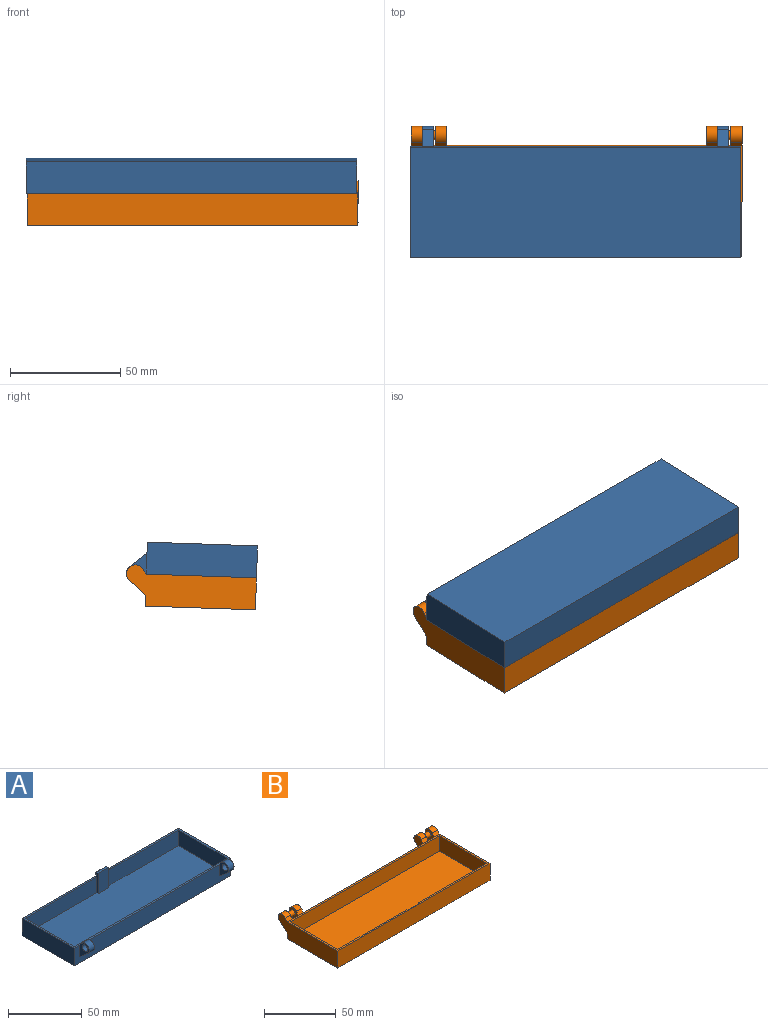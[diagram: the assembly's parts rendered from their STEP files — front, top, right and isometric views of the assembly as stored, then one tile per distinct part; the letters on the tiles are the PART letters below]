
ASSEMBLY  parts=2 mates=1
PART A: 32 faces, bbox 150x59x18.5 mm
  f0: plane 10x2mm, normal (0,1,0), area 20mm2, adj f1,f11,f13,f17
  f1: plane 150x50mm, normal (0,0,1), area 591mm2, adj f0,f2,f3,f4,f5,f7,f8,f9
  f2: plane 150x14.5mm, normal (0,-1,0), area 2080.2mm2, adj f1,f3,f5,f6,f22,f23,f24,f29
  f3: plane 50x14.5mm, normal (1,0,0), area 725mm2, adj f1,f2,f4,f6
  f4: plane 150x14.5mm, normal (0,1,0), area 2175mm2, adj f1,f3,f5,f6
  f5: plane 50x14.5mm, normal (-1,0,0), area 725mm2, adj f1,f2,f4,f6
  f6: plane 150x50mm, normal (0,0,-1), area 7500mm2, adj f2,f3,f4,f5
  f7: plane 47x13mm, normal (-1,0,0), area 611mm2, adj f1,f8,f14,f15
  f8: plane 147x13mm, normal (0,1,0), area 1911mm2, adj f1,f7,f9,f15
  f9: plane 47x13mm, normal (1,0,0), area 611mm2, adj f1,f8,f10,f15
  f10: plane 68.5x13mm, normal (0,-1,0), area 890.5mm2, adj f1,f9,f11,f15
  f11: plane 17x2.5mm, normal (-1,0,0), area 27.1mm2, adj f0,f10,f12,f15,f16,f17
  f12: plane 17x10mm, normal (0,-1,0), area 170mm2, adj f11,f13,f15,f16
  f13: plane 17x2.5mm, normal (1,0,0), area 27.1mm2, adj f0,f12,f14,f15,f16,f17
  f14: plane 68.5x13mm, normal (0,-1,0), area 890.5mm2, adj f1,f7,f13,f15
  f15: plane 147x47mm, normal (0,0,1), area 6894mm2, adj f7,f8,f9,f10,f11,f12,f13,f14
  f16: plane 10x1.5mm, normal (0,0,1), area 15mm2, adj f11,f12,f13,f17
  f17: cylinder r=1mm len=10mm, axis (1,0,0), area 31.4mm2, adj f0,f11,f13,f16
  f18: plane 5x0mm, normal (0,1,0), area 0mm2, adj f1,f19,f23,f24
  f19: plane 5x2.4mm, normal (0,0.8,0.6), area 15mm2, adj f18,f20,f23,f24
  f20: cylinder r=4mm len=7.2mm, axis (1,0,0), area 67.3mm2, adj f19,f22,f23,f24
  f21: cylinder r=2.5mm len=5mm, axis (1,0,0), area 78.5mm2, adj f23,f24
  f22: plane 7.59x6.42mm, normal (0,-0.65,-0.76), area 49.7mm2, adj f2,f20,f23,f24
  f23: plane 13.48x9mm, normal (1,0,0), area 56.9mm2, adj f1,f2,f18,f19,f20,f21,f22
  f24: plane 13.48x9mm, normal (-1,0,0), area 56.9mm2, adj f1,f2,f18,f19,f20,f21,f22
  f25: plane 5x0mm, normal (0,1,0), area 0mm2, adj f1,f26,f30,f31
  f26: plane 5x2.4mm, normal (0,0.8,0.6), area 15mm2, adj f25,f27,f30,f31
  f27: cylinder r=4mm len=7.2mm, axis (-1,0,0), area 67.3mm2, adj f26,f29,f30,f31
  f28: cylinder r=2.5mm len=5mm, axis (-1,0,0), area 78.5mm2, adj f30,f31
  f29: plane 7.59x6.42mm, normal (0,-0.65,-0.76), area 49.7mm2, adj f2,f27,f30,f31
  f30: plane 13.48x9mm, normal (-1,0,0), area 56.9mm2, adj f1,f2,f25,f26,f27,f28,f29
  f31: plane 13.48x9mm, normal (1,0,0), area 56.9mm2, adj f1,f2,f25,f26,f27,f28,f29
PART B: 39 faces, bbox 150x59x18.5 mm
  f0: plane 150x14.5mm, normal (0,-1,0), area 2175mm2, adj f1,f3,f4,f9
  f1: plane 59x18.5mm, normal (1,0,0), area 801.6mm2, adj f0,f2,f4,f9,f17,f18,f19
  f2: plane 150x14.5mm, normal (0,1,0), area 1988.2mm2, adj f1,f3,f4,f9,f17,f20,f21,f22
  f3: plane 59x18.5mm, normal (-1,0,0), area 801.6mm2, adj f0,f2,f4,f9,f28,f29,f30
  f4: plane 150x50mm, normal (0,0,-1), area 7500mm2, adj f0,f1,f2,f3
  f5: plane 47x13mm, normal (-1,0,0), area 611mm2, adj f6,f8,f9,f10
  f6: plane 147x13mm, normal (0,1,0), area 1867.8mm2, adj f5,f7,f9,f10,f11,f12,f13,f14
  f7: plane 47x13mm, normal (1,0,0), area 611mm2, adj f6,f8,f9,f10
  f8: plane 147x13mm, normal (0,-1,0), area 1911mm2, adj f5,f7,f9,f10
  f9: plane 150x50mm, normal (0,0,1), area 582mm2, adj f0,f1,f2,f3,f5,f6,f7,f8
  f10: plane 147x47mm, normal (0,0,1), area 6909mm2, adj f5,f6,f7,f8
  f11: plane 12x1.5mm, normal (0,0.89,0.45), area 20.1mm2, adj f6,f9,f12,f13
  f12: plane 1.5x0.75mm, normal (-1,0,0), area 0.6mm2, adj f6,f9,f11
  f13: plane 1.5x0.75mm, normal (1,0,0), area 0.6mm2, adj f6,f9,f11
  f14: cylinder r=1.05mm len=12mm, axis (1,0,0), area 39.6mm2, adj f6,f15,f16
  f15: plane 2.1x1.05mm, normal (-1,0,0), area 1.7mm2, adj f6,f14
  f16: plane 2.1x1.05mm, normal (1,0,0), area 1.7mm2, adj f6,f14
  f17: plane 7.59x6.45mm, normal (0,0.65,-0.76), area 49.8mm2, adj f1,f2,f18,f20
  f18: cylinder r=4mm len=7.2mm, axis (1,0,0), area 67.3mm2, adj f1,f17,f19,f20
  f19: plane 5x2.4mm, normal (0,-0.8,0.6), area 15mm2, adj f1,f9,f18,f20
  f20: plane 13.5x9mm, normal (-1,0,0), area 64mm2, adj f2,f17,f18,f19,f27
  f21: plane 5x0.16mm, normal (0,-1,0.02), area 0.8mm2, adj f2,f24,f25,f26
  f22: plane 7.56x6.28mm, normal (0,0.64,-0.77), area 49.1mm2, adj f2,f23,f25,f26
  f23: cylinder r=4mm len=7.21mm, axis (1,0,0), area 67.6mm2, adj f22,f24,f25,f26
  f24: plane 5x2.4mm, normal (0,-0.8,0.6), area 15mm2, adj f21,f23,f25,f26
  f25: plane 13.35x9mm, normal (1,0,0), area 63.5mm2, adj f2,f21,f22,f23,f24,f27
  f26: plane 13.35x9mm, normal (-1,0,0), area 76mm2, adj f2,f21,f22,f23,f24
  f27: cylinder r=2mm len=6mm, axis (1,0,0), area 75.4mm2, adj f20,f25
  f28: plane 7.59x6.45mm, normal (0,0.65,-0.76), area 49.8mm2, adj f2,f3,f29,f31
  f29: cylinder r=4mm len=7.2mm, axis (-1,0,0), area 67.3mm2, adj f3,f28,f30,f31
  f30: plane 5x2.4mm, normal (0,-0.8,0.6), area 15mm2, adj f3,f9,f29,f31
  f31: plane 13.5x9mm, normal (1,0,0), area 64mm2, adj f2,f28,f29,f30,f38
  f32: plane 5x0.16mm, normal (0,-1,0.02), area 0.8mm2, adj f2,f35,f36,f37
  f33: plane 7.56x6.28mm, normal (0,0.64,-0.77), area 49.1mm2, adj f2,f34,f36,f37
  f34: cylinder r=4mm len=7.21mm, axis (-1,0,0), area 67.6mm2, adj f33,f35,f36,f37
  f35: plane 5x2.4mm, normal (0,-0.8,0.6), area 15mm2, adj f32,f34,f36,f37
  f36: plane 13.35x9mm, normal (-1,0,0), area 63.5mm2, adj f2,f32,f33,f34,f35,f38
  f37: plane 13.35x9mm, normal (1,0,0), area 76mm2, adj f2,f32,f33,f34,f35
  f38: cylinder r=2mm len=6mm, axis (-1,0,0), area 75.4mm2, adj f31,f36
PLACE A rot(axis=(-1,0,0),178.1deg) t=(-0.26,76.43,31.57)mm
PLACE B rot(axis=(1,0,0),1.9deg) t=(0.24,-32.53,-1.15)mm
MATE revolute A.f27 <-> B.f23  axis (-1,0,0) through (139.24,21.95,15.21)mm
